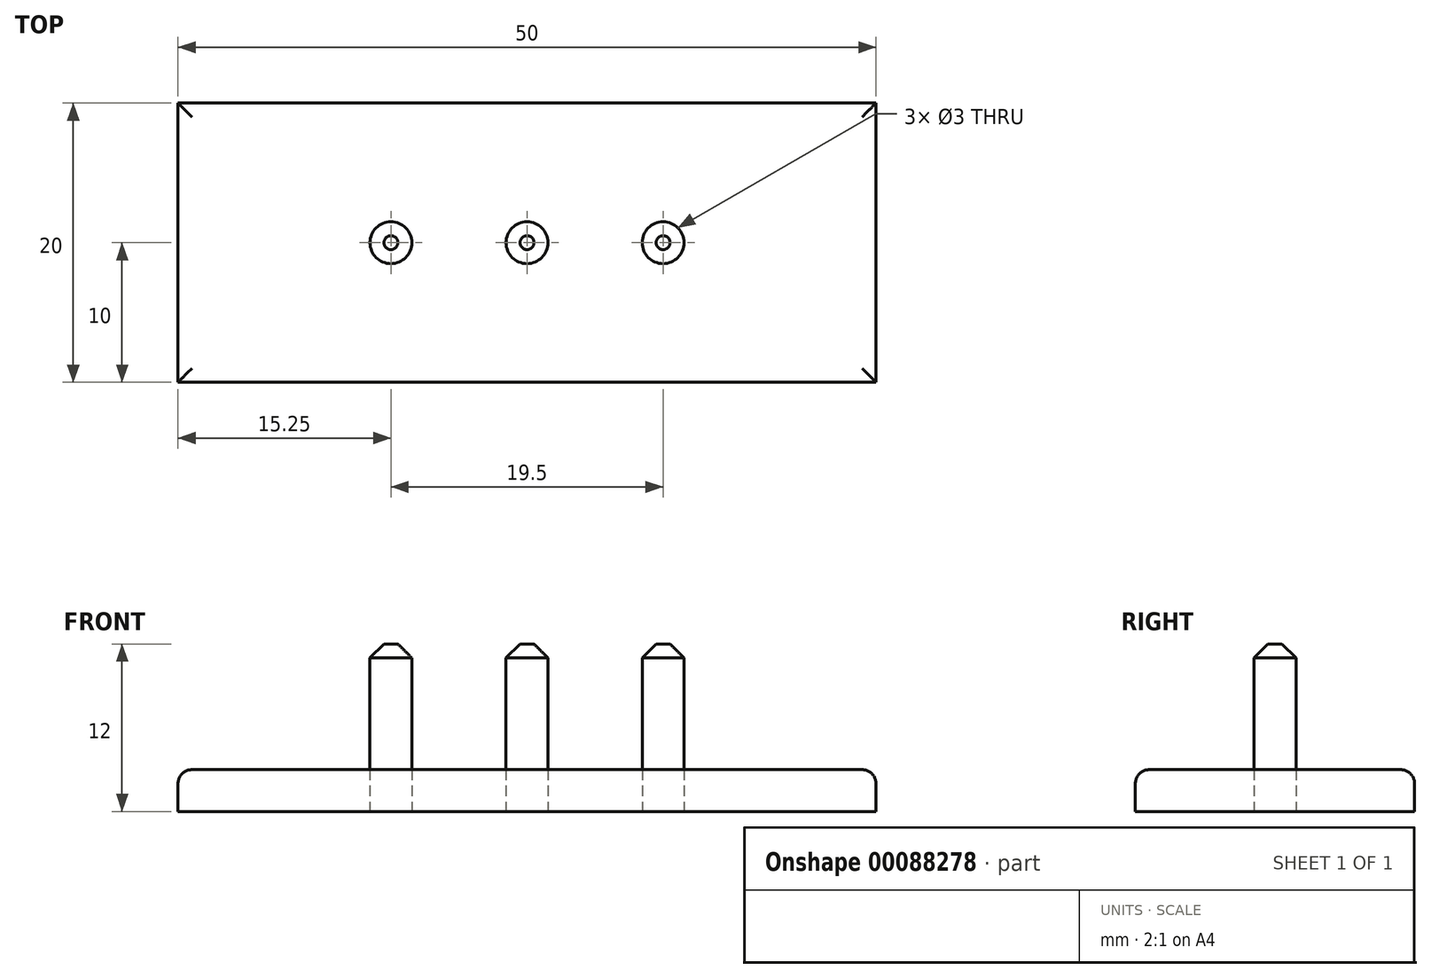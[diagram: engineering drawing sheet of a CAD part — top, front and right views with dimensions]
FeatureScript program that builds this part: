
annotation { "Feature Type Name" : "Feature", "Feature Type Description" : "" }
export const myFeature = defineFeature(function(context is Context, id is Id, definition is map)
    precondition{}
    {
        {
            var Q0;
            Q0=qCreatedBy(makeId("Top.planeOp"),FACE);
            var sketch = newSketch(context, id + "F0", { "sketchPlane" : qUnion([Q0])});
            skLineSegment(sketch, "E0.bottom", {"start": v(0, 0) * mm, "end": v(50, 0) * mm});
            skLineSegment(sketch, "E0.top", {"start": v(0, 20) * mm, "end": v(50, 20) * mm});
            skLineSegment(sketch, "E0.left", {"start": v(0, 0) * mm, "end": v(0, 20) * mm});
            skLineSegment(sketch, "E0.right", {"start": v(50, 0) * mm, "end": v(50, 20) * mm});
            skPoint(sketch, "E1", {"position": v(25, 10) * mm});
            skPoint(sketch, "E1.positionSnap0", {"position": v(50, 10) * mm});
            skPoint(sketch, "E1.positionSnap1", {"position": v(25, 0) * mm});
            skPoint(sketch, "E2", {"position": v(34.75, 10) * mm});
            skPoint(sketch, "E3", {"position": v(15.25, 10) * mm});
            skCircle(sketch, "E4", {"center": v(15.25, 10) * mm, "radius": 1.5 * mm});
            skCircle(sketch, "E5", {"center": v(25, 10) * mm, "radius": 1.5 * mm});
            skCircle(sketch, "E6", {"center": v(34.75, 10) * mm, "radius": 1.5 * mm});
            skSolve(sketch);
        }
        {
            var Q0;
            Q0=makeQuery(id+"F0.imprint","IMPRINT",FACE,{"disambiguationData":[TD([[makeQuery(id+"F0.imprint","IMPRINT",EDGE,{"derivedFrom":sQuery(id+"F0.wireOp",EDGE,"E6")}),1.0]])]});
            var Q1;
            Q1=makeQuery(id+"F0.imprint","IMPRINT",FACE,{"disambiguationData":[TD([[makeQuery(id+"F0.imprint","IMPRINT",EDGE,{"derivedFrom":sQuery(id+"F0.wireOp",EDGE,"E5")}),1.0]])]});
            var Q2;
            Q2=makeQuery(id+"F0.imprint","IMPRINT",FACE,{"disambiguationData":[TD([[makeQuery(id+"F0.imprint","IMPRINT",EDGE,{"derivedFrom":sQuery(id+"F0.wireOp",EDGE,"E4")}),1.0]])]});
            var Q3;
            Q3=sQuery(id+"F0.wireOp",EDGE,"E6");
            var Q4;
            Q4=sQuery(id+"F0.wireOp",EDGE,"E5");
            var Q5;
            Q5=sQuery(id+"F0.wireOp",EDGE,"E4");
            extrude(context, id + "F1", {"entities" : qUnion([Q0, Q1, Q2]), "surfaceEntities" : qUnion([Q3, Q4, Q5]), "depth" : 12 * mm});
        }
        {
            var Q0;
            Q0=makeQuery(id+"F0.imprint","IMPRINT",FACE,{"disambiguationData":[TD([[makeQuery(id+"F0.imprint","IMPRINT",EDGE,{"derivedFrom":sQuery(id+"F0.wireOp",EDGE,"E0.bottom")}),1.0]])]});
            extrude(context, id + "F2", {"entities" : qUnion([Q0]), "depth" : 3 * mm});
        }
        {
            var Q0;
            Q0=makeQuery(id+"F2.opExtrude","CAP_EDGE",EDGE,{"disambiguationData":[OSD([sQuery(id+"F0.wireOp",EDGE,"E0.bottom")])],"isStart":false});
            var Q1;
            Q1=makeQuery(id+"F2.opExtrude","CAP_EDGE",EDGE,{"disambiguationData":[OSD([sQuery(id+"F0.wireOp",EDGE,"E0.left")])],"isStart":false});
            var Q2;
            Q2=makeQuery(id+"F2.opExtrude","CAP_EDGE",EDGE,{"disambiguationData":[OSD([sQuery(id+"F0.wireOp",EDGE,"E0.top")])],"isStart":false});
            var Q3;
            Q3=makeQuery(id+"F2.opExtrude","CAP_EDGE",EDGE,{"disambiguationData":[OSD([sQuery(id+"F0.wireOp",EDGE,"E0.right")])],"isStart":false});
            fillet(context, id + "F3", {"entities" : qUnion([Q0, Q1, Q2, Q3]), "radius" : 1 * mm, "tangentPropagation" : true, "allowEdgeOverflow" : false});
        }
        {
            var Q0;
            Q0=makeQuery(id+"F1.opExtrude","CAP_EDGE",EDGE,{"disambiguationData":[OSD([sQuery(id+"F0.wireOp",EDGE,"E6")])],"isStart":false});
            var Q1;
            Q1=makeQuery(id+"F1.opExtrude","CAP_EDGE",EDGE,{"disambiguationData":[OSD([sQuery(id+"F0.wireOp",EDGE,"E5")])],"isStart":false});
            var Q2;
            Q2=makeQuery(id+"F1.opExtrude","CAP_EDGE",EDGE,{"disambiguationData":[OSD([sQuery(id+"F0.wireOp",EDGE,"E4")])],"isStart":false});
            chamfer(context, id + "F4", {"entities" : qUnion([Q0, Q1, Q2]), "width" : 1 * mm, "tangentPropagation" : true});
        }
    });
